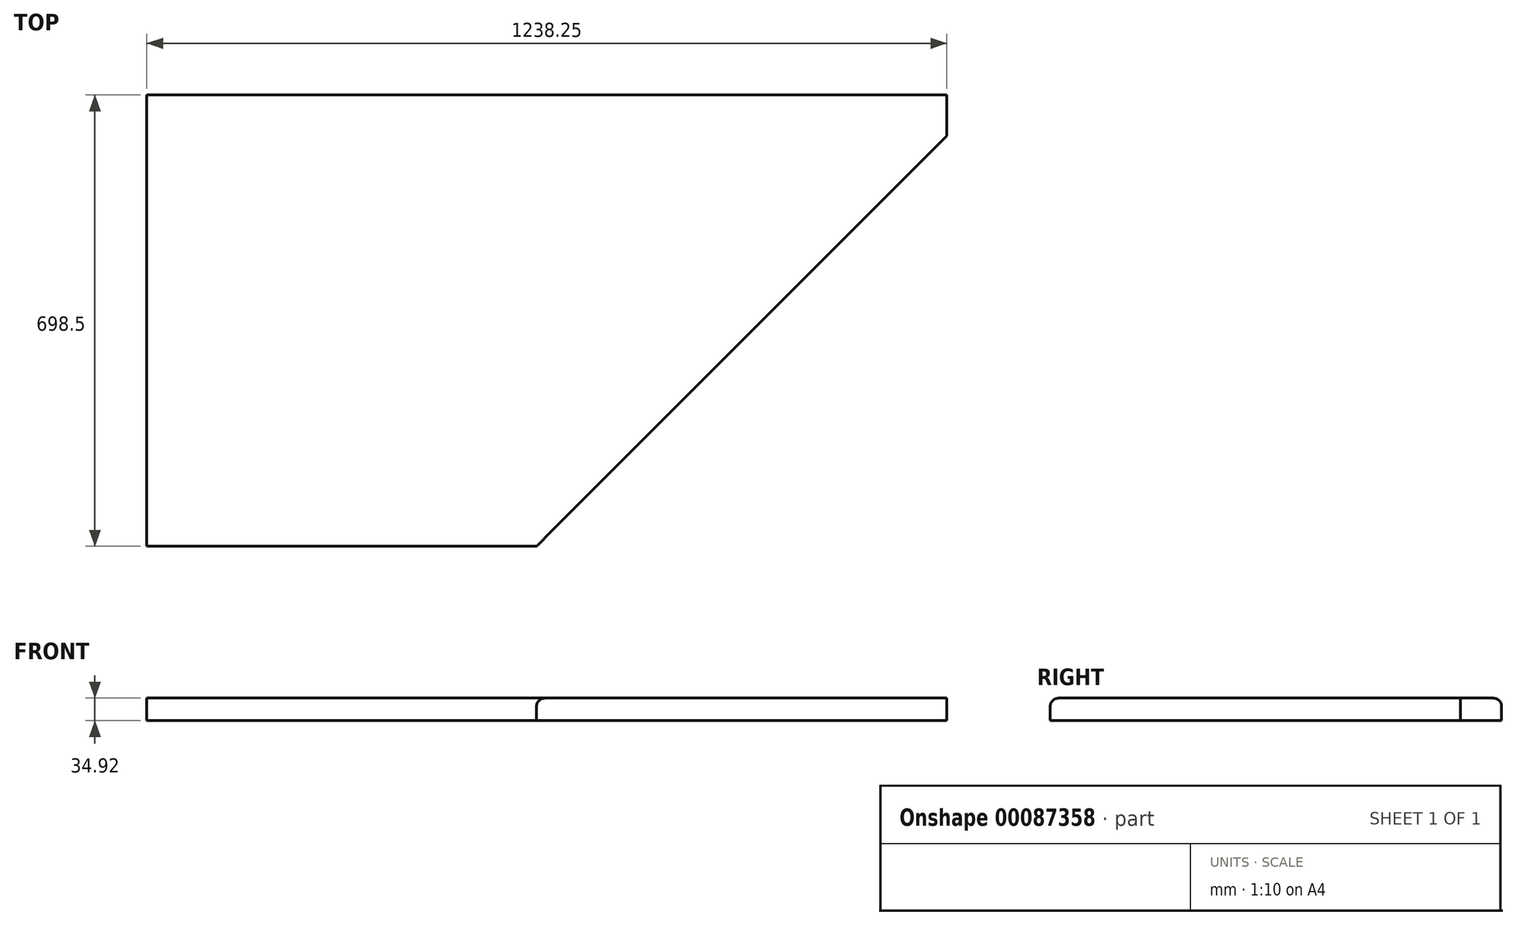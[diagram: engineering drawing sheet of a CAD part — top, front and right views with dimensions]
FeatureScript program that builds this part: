
annotation { "Feature Type Name" : "Feature", "Feature Type Description" : "" }
export const myFeature = defineFeature(function(context is Context, id is Id, definition is map)
    precondition{}
    {
        {
            var Q0;
            Q0=qCreatedBy(makeId("Right.planeOp"),FACE);
            var sketch = newSketch(context, id + "F0", { "sketchPlane" : qUnion([Q0])});
            skLineSegment(sketch, "E0.bottom", {"start": v(0, 0) * mm, "end": v(-698.5, 0) * mm});
            skLineSegment(sketch, "E0.top", {"start": v(-12.7, 34.92) * mm, "end": v(-685.8, 34.92) * mm});
            skLineSegment(sketch, "E0.left", {"start": v(0, 0) * mm, "end": v(0, 22.22) * mm});
            skLineSegment(sketch, "E0.right", {"start": v(-698.5, 0) * mm, "end": v(-698.5, 22.22) * mm});
            skPoint(sketch, "E1.visualSharp", {"position": v(-698.5, 34.92) * mm});
            skArc(sketch, "E1.filletArc", {"start": v(-685.8, 34.92) * mm, "mid": v(-694.78, 31.2) * mm, "end": v(-698.5, 22.22) * mm});
            skPoint(sketch, "E2.visualSharp", {"position": v(0, 34.92) * mm});
            skArc(sketch, "E2.filletArc", {"start": v(0, 22.22) * mm, "mid": v(-3.72, 31.2) * mm, "end": v(-12.7, 34.93) * mm});
            skSolve(sketch);
        }
        {
            var Q0;
            Q0 = qSketchRegion(id + "F0", true);
            extrude(context, id + "F1", {"entities" : qUnion([Q0]), "depth" : 1238.25 * mm});
        }
        {
            var Q0;
            Q0=makeQuery(id+"F1.opExtrude","SWEPT_FACE",FACE,{"disambiguationData":[OSD([sQuery(id+"F0.wireOp",EDGE,"E0.bottom")])]});
            var sketch = newSketch(context, id + "F2", { "sketchPlane" : qUnion([Q0])});
            skLineSegment(sketch, "E3", {"start": v(1238.25, 63.5) * mm, "end": v(1238.25, 698.5) * mm});
            skLineSegment(sketch, "E4", {"start": v(1238.25, 698.5) * mm, "end": v(603.25, 698.5) * mm});
            skLineSegment(sketch, "E5", {"start": v(603.25, 698.5) * mm, "end": v(1238.25, 63.5) * mm});
            skSolve(sketch);
        }
        {
            var Q0;
            Q0 = qSketchRegion(id + "F2", true);
            extrude(context, id + "F3", {"entities" : qUnion([Q0]), "operationType" : NewBodyOperationType.REMOVE, "oppositeDirection" : true, "depth" : 127 * mm});
        }
    });
